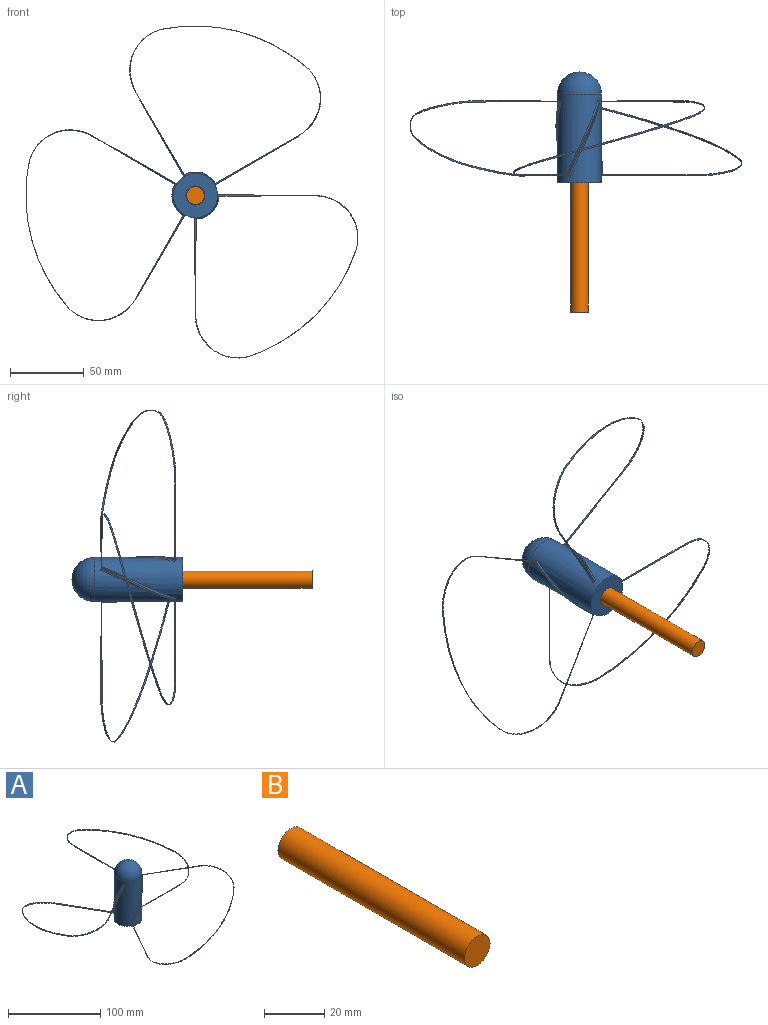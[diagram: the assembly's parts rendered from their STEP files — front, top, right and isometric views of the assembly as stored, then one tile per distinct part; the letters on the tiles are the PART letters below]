
ASSEMBLY  parts=2 mates=1
PART A: 26 faces, bbox 236.2x236.2x75.9 mm
  f0: cylinder r=15mm len=60mm, axis (0,0,-1), area 5182mm2, adj f1,f3,f4,f5,f6,f7,f15,f16
  f1: bspline ~73.9x43.67mm, area 65.7mm2, adj f0,f6,f7,f8
  f2: bspline ~101.74x31.17mm, area 107.2mm2, adj f8,f9
  f3: bspline ~73.9x43.67mm, area 65.7mm2, adj f0,f6,f7,f9
  f4: plane 30x30mm, normal (0,0,-1), area 574.1mm2, adj f0,f10
  f5: sphere r=15mm, area 1413.7mm2, adj f0
  f6: bspline ~55.4x23.65mm, area 83mm2, adj f0,f1,f3
  f7: bspline ~52.18x22.2mm, area 83mm2, adj f0,f1,f3
  f8: bspline ~47.85x35mm, area 56.9mm2, adj f1,f2
  f9: bspline ~43.55x38.42mm, area 56.9mm2, adj f2,f3
  f10: cylinder r=6.5mm len=20.5mm, axis (0,0,-1), area 837.2mm2, adj f4,f11
  f11: plane 13x13mm, normal (0,0,-1), area 132.7mm2, adj f10
  f12: bspline ~101.74x31.17mm, area 107.2mm2, adj f13,f14
  f13: bspline ~43.55x38.42mm, area 56.9mm2, adj f12,f16
  f14: bspline ~47.85x35mm, area 56.9mm2, adj f12,f15
  f15: bspline ~73.9x43.67mm, area 65.7mm2, adj f0,f14,f17,f18
  f16: bspline ~73.9x43.67mm, area 65.7mm2, adj f0,f13,f17,f18
  f17: bspline ~52.18x22.7mm, area 83mm2, adj f0,f15,f16
  f18: bspline ~55.4x23.33mm, area 83mm2, adj f0,f15,f16
  f19: bspline ~84.33x2.71mm, area 65.7mm2, adj f0,f22,f23,f24
  f20: bspline ~74.48x74.48mm, area 107.2mm2, adj f24,f25
  f21: bspline ~84.33x2.71mm, area 65.7mm2, adj f0,f22,f23,f25
  f22: bspline ~55.4x18.2mm, area 83mm2, adj f0,f19,f21
  f23: bspline ~52.18x17.61mm, area 83mm2, adj f0,f19,f21
  f24: bspline ~41.14x39.47mm, area 56.9mm2, adj f19,f20
  f25: bspline ~41.14x39.47mm, area 56.9mm2, adj f20,f21
PART B: 3 faces, bbox 12x87.8x12 mm
  f0: cylinder r=6mm len=87.8mm, axis (0,1,0), area 3310mm2, adj f1,f2
  f1: plane 12x12mm, normal (0,-1,0), area 113.1mm2, adj f0
  f2: plane 12x12mm, normal (0,1,0), area 113.1mm2, adj f0
PLACE A rot(axis=(-1,0,0),90deg) t=(24.63,-149.96,-64.46)mm
PLACE B t=(24.63,-154.96,-64.46)mm
MATE revolute A.f0 <-> B.f0  axis (0,-1,0) through (24.63,-154.96,-64.46)mm
